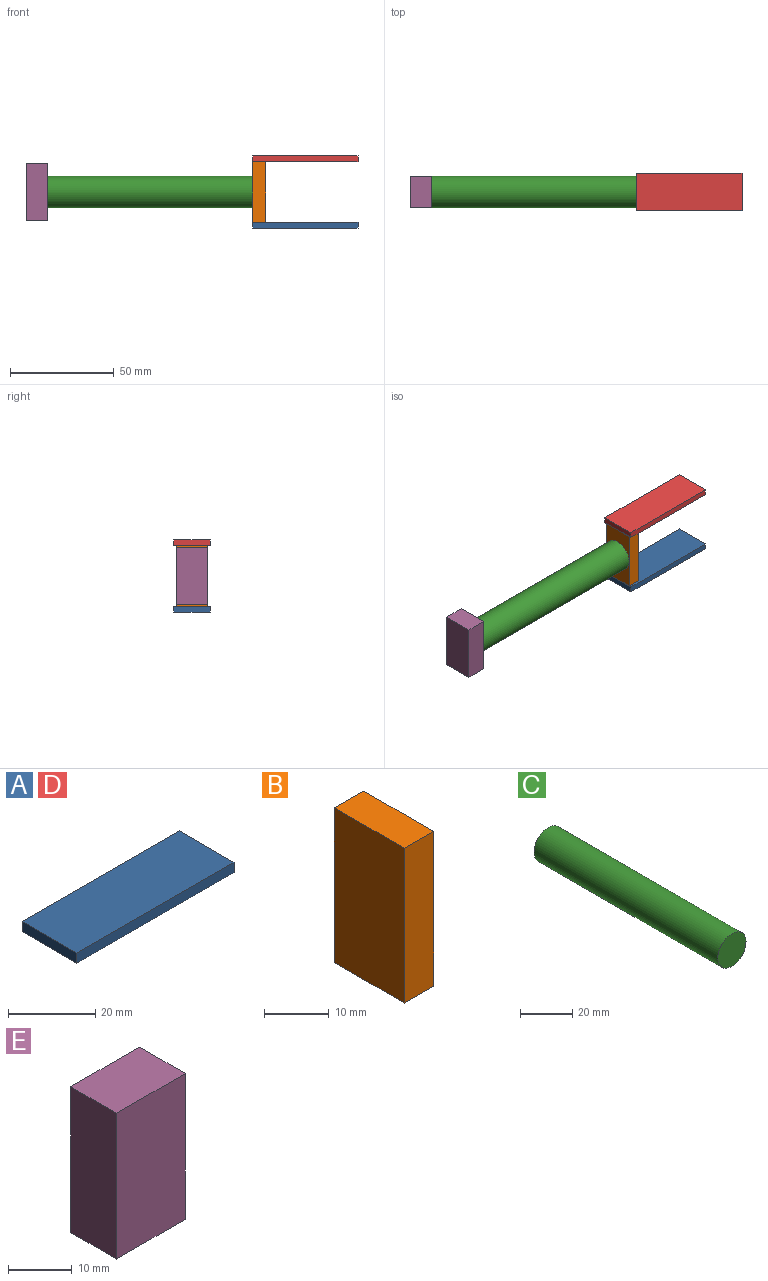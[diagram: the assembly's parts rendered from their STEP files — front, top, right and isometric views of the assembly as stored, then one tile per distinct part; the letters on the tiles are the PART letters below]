
ASSEMBLY  parts=5 mates=4
PART A: 6 faces, bbox 50.8x17.8x2.8 mm
  f0: plane 50.8x17.78mm, normal (0,0,1), area 903.2mm2, adj f1,f3,f4,f5
  f1: plane 17.78x2.82mm, normal (-1,0,0), area 50.2mm2, adj f0,f2,f4,f5
  f2: plane 50.8x17.78mm, normal (0,0,-1), area 903.2mm2, adj f1,f3,f4,f5
  f3: plane 17.78x2.82mm, normal (1,0,0), area 50.2mm2, adj f0,f2,f4,f5
  f4: plane 50.8x2.82mm, normal (0,-1,0), area 143.4mm2, adj f0,f1,f2,f3
  f5: plane 50.8x2.82mm, normal (0,1,0), area 143.4mm2, adj f0,f1,f2,f3
PART B: 6 faces, bbox 6.4x15.2x29.2 mm
  f0: plane 29.21x15.24mm, normal (-1,0,0), area 445.2mm2, adj f1,f3,f4,f5
  f1: plane 15.24x6.35mm, normal (0,0,-1), area 96.8mm2, adj f0,f2,f4,f5
  f2: plane 29.21x15.24mm, normal (1,0,0), area 445.2mm2, adj f1,f3,f4,f5
  f3: plane 15.24x6.35mm, normal (0,0,1), area 96.8mm2, adj f0,f2,f4,f5
  f4: plane 29.21x6.35mm, normal (0,-1,0), area 185.5mm2, adj f0,f1,f2,f3
  f5: plane 29.21x6.35mm, normal (0,1,0), area 185.5mm2, adj f0,f1,f2,f3
PART C: 3 faces, bbox 15.2x99.1x15.2 mm
  f0: cylinder r=7.62mm len=99.06mm, axis (0,1,0), area 4742.8mm2, adj f1,f2
  f1: plane 15.24x15.24mm, normal (0,-1,0), area 182.4mm2, adj f0
  f2: plane 15.24x15.24mm, normal (0,1,0), area 182.4mm2, adj f0
PART D: same geometry as A
PART E: 6 faces, bbox 15.2x10.2x27.9 mm
  f0: plane 27.94x10.16mm, normal (-1,0,0), area 283.9mm2, adj f1,f3,f4,f5
  f1: plane 15.24x10.16mm, normal (0,0,-1), area 154.8mm2, adj f0,f2,f4,f5
  f2: plane 27.94x10.16mm, normal (1,0,0), area 283.9mm2, adj f1,f3,f4,f5
  f3: plane 15.24x10.16mm, normal (0,0,1), area 154.8mm2, adj f0,f2,f4,f5
  f4: plane 27.94x15.24mm, normal (0,-1,0), area 425.8mm2, adj f0,f1,f2,f3
  f5: plane 27.94x15.24mm, normal (0,1,0), area 425.8mm2, adj f0,f1,f2,f3
PLACE A t=(-22.67,6.74,-24.75)mm
PLACE B t=(-18.91,5.47,9.05)mm
PLACE C rot(axis=(0,0,-1),90deg) t=(-18.91,-2.15,23.66)mm
PLACE D t=(-22.67,6.74,7.28)mm
PLACE E rot(axis=(0,0,1),90deg) t=(-128.13,-9.77,9.69)mm
MATE fastened A.f0 <-> B.f1  axis (0,0,1) through (-18.91,-2.15,9.05)mm
MATE fastened C.f0 <-> B.f0  axis (1,0,0) through (-18.91,-2.15,23.66)mm
MATE fastened E.f4 <-> C.f0  axis (1,0,0) through (-117.97,-2.15,23.66)mm
MATE fastened B.f3 <-> D.f2  axis (0,0,1) through (-18.91,-2.15,38.26)mm
